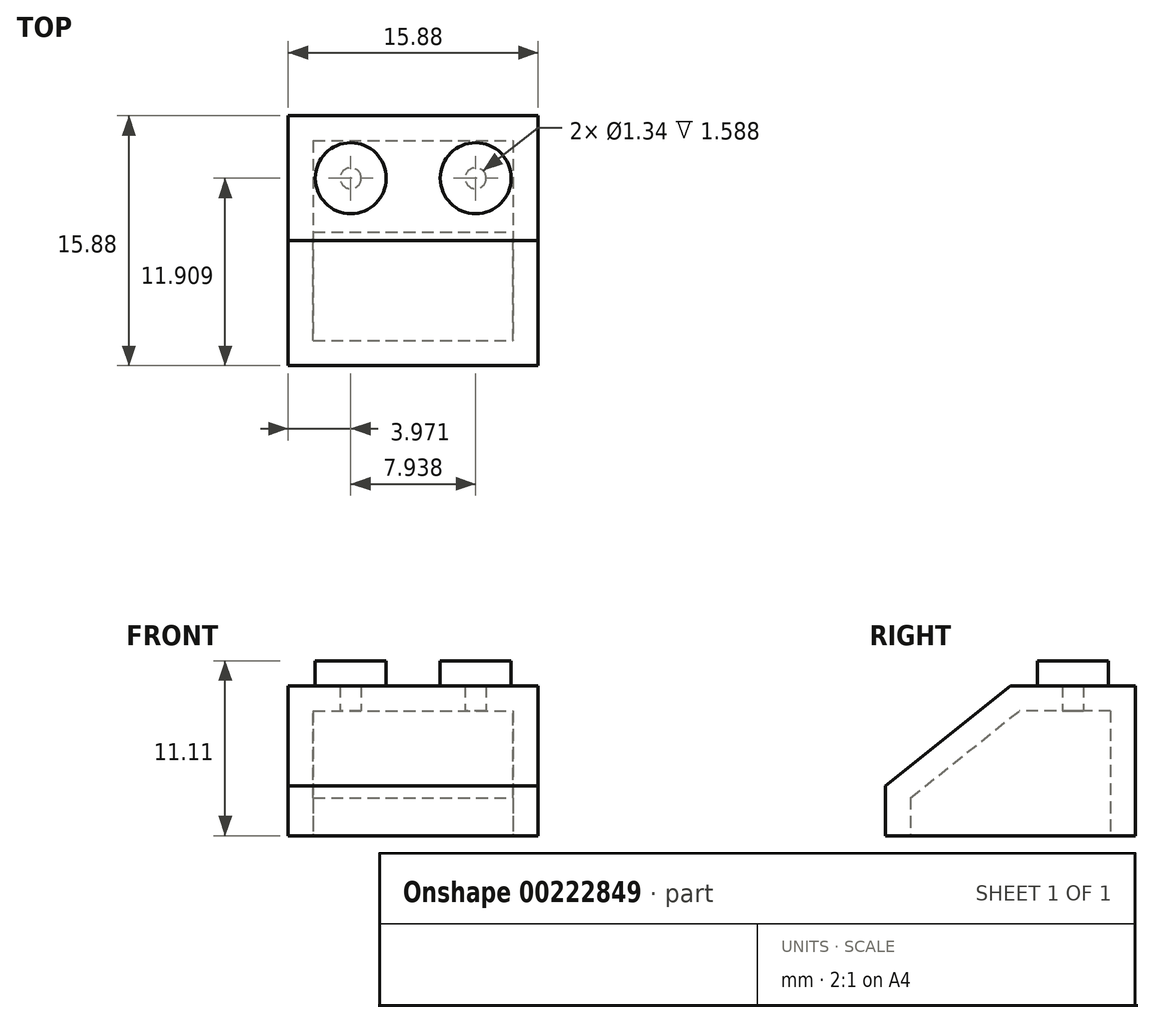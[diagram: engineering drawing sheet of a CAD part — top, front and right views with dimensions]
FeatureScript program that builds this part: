
annotation { "Feature Type Name" : "Feature", "Feature Type Description" : "" }
export const myFeature = defineFeature(function(context is Context, id is Id, definition is map)
    precondition{}
    {
        {
            var Q0;
            Q0=qCreatedBy(makeId("Top.planeOp"),FACE);
            var sketch = newSketch(context, id + "F0", { "sketchPlane" : qUnion([Q0])});
            skLineSegment(sketch, "E0.bottom", {"start": v(-7.94, 7.94) * mm, "end": v(7.94, 7.94) * mm});
            skLineSegment(sketch, "E0.top", {"start": v(-7.94, -7.94) * mm, "end": v(7.94, -7.94) * mm});
            skLineSegment(sketch, "E0.left", {"start": v(-7.94, 7.94) * mm, "end": v(-7.94, -7.94) * mm});
            skLineSegment(sketch, "E0.right", {"start": v(7.94, 7.94) * mm, "end": v(7.94, -7.94) * mm});
            skPoint(sketch, "E0.middle", {"position": v(0, 0) * mm});
            skCircle(sketch, "E1", {"center": v(-3.97, 3.97) * mm, "radius": 2.26 * mm});
            skCircle(sketch, "E2.1.0.0", {"center": v(3.97, 3.97) * mm, "radius": 2.26 * mm});
            skLineSegment(sketch, "E2.direction1", {"start": v(-3.97, 3.97) * mm, "end": v(3.97, 3.97) * mm, "construction": true});
            skLineSegment(sketch, "E2.direction2", {"start": v(-3.97, 3.97) * mm, "end": v(-3.97, -3.97) * mm, "construction": true});
            skCircle(sketch, "E3", {"center": v(0, 0) * mm, "radius": 3.18 * mm});
            skCircle(sketch, "E4.0", {"center": v(0, 0) * mm, "radius": 2.38 * mm});
            skSolve(sketch);
        }
        {
            var Q0;
            Q0 = qSketchRegion(id + "F0", true);
            var Q1;
            Q1=makeQuery(id+"F0.imprint","IMPRINT",FACE,{"disambiguationData":[TD([[makeQuery(id+"F0.imprint","IMPRINT",EDGE,{"derivedFrom":sQuery(id+"F0.wireOp",EDGE,"E4.0")}),1.0]])]});
            var Q2;
            Q2=makeQuery(id+"F0.imprint","IMPRINT",FACE,{"disambiguationData":[TD([[makeQuery(id+"F0.imprint","IMPRINT",EDGE,{"derivedFrom":sQuery(id+"F0.wireOp",EDGE,"E3")}),1.0]])]});
            extrude(context, id + "F1", {"entities" : qUnion([Q0, Q1, Q2]), "depth" : 9.52 * mm});
        }
        {
            var Q0;
            Q0=makeQuery(id+"F0.imprint","IMPRINT",FACE,{"disambiguationData":[TD([[makeQuery(id+"F0.imprint","IMPRINT",EDGE,{"derivedFrom":sQuery(id+"F0.wireOp",EDGE,"E1")}),1.0]])]});
            var Q1;
            Q1=makeQuery(id+"F0.imprint","IMPRINT",FACE,{"disambiguationData":[TD([[makeQuery(id+"F0.imprint","IMPRINT",EDGE,{"derivedFrom":sQuery(id+"F0.wireOp",EDGE,"E2.1.0.0")}),1.0]])]});
            extrude(context, id + "F2", {"entities" : qUnion([Q0, Q1]), "operationType" : NewBodyOperationType.ADD, "depth" : 11.1 * mm});
        }
        {
            var Q0;
            Q0=makeQuery(id+"F0.imprint","IMPRINT",FACE,{"disambiguationData":[TD([[makeQuery(id+"F0.imprint","IMPRINT",EDGE,{"derivedFrom":sQuery(id+"F0.wireOp",EDGE,"E3")}),1.0]])]});
            extrude(context, id + "F3", {"entities" : qUnion([Q0]), "operationType" : NewBodyOperationType.ADD, "depth" : 9.52 * mm});
        }
        {
            var Q0;
            Q0=makeQuery(id+"F1.opExtrude","SWEPT_FACE",FACE,{"disambiguationData":[OSD([sQuery(id+"F0.wireOp",EDGE,"E0.right")])]});
            var sketch = newSketch(context, id + "F4", { "sketchPlane" : qUnion([Q0])});
            skPoint(sketch, "E5", {"position": v(0, 9.53) * mm});
            skPoint(sketch, "E6", {"position": v(-7.94, 3.18) * mm});
            skLineSegment(sketch, "E7", {"start": v(-7.94, 3.17) * mm, "end": v(0, 9.53) * mm});
            skSolve(sketch);
        }
        {
            var Q0;
            {var subQ0=sQuery(id+"F4.wireOp",EDGE,"E7");Q0=makeQuery(id+"F4.imprint","IMPRINT",FACE,{"disambiguationData":[TD([[makeQuery(id+"F4.imprint","IMPRINT",EDGE,{"derivedFrom":subQ0}),1.0]])]});}
            extrude(context, id + "F5", {"entities" : qUnion([Q0]), "operationType" : NewBodyOperationType.REMOVE, "oppositeDirection" : true, "depth" : 25.4 * mm});
        }
        {
            var Q0;
            {var subQ0=sQuery(id+"F0.wireOp",EDGE,"E2.1.0.0");var subQ1=sQuery(id+"F0.wireOp",EDGE,"E1");Q0=makeQuery(id+"F2.boolean.opBoolean","MERGE",FACE,{"derivedFrom":[makeQuery(id+"F1.opExtrude","CAP_FACE",FACE,{"disambiguationData":[OSD([sQuery(id+"F0.wireOp",EDGE,"E0.bottom"),sQuery(id+"F0.wireOp",EDGE,"E0.top"),sQuery(id+"F0.wireOp",EDGE,"E0.left"),sQuery(id+"F0.wireOp",EDGE,"E0.right"),subQ1,subQ0])],"isStart":true}),makeQuery(id+"F2.opExtrude","CAP_FACE",FACE,{"disambiguationData":[OSD([subQ1])],"isStart":true}),makeQuery(id+"F2.opExtrude","CAP_FACE",FACE,{"disambiguationData":[OSD([subQ0])],"isStart":true})]});}
            shell(context, id + "F6", {"entities" : qUnion([Q0]), "thickness" : 1.59 * mm});
        }
    });
